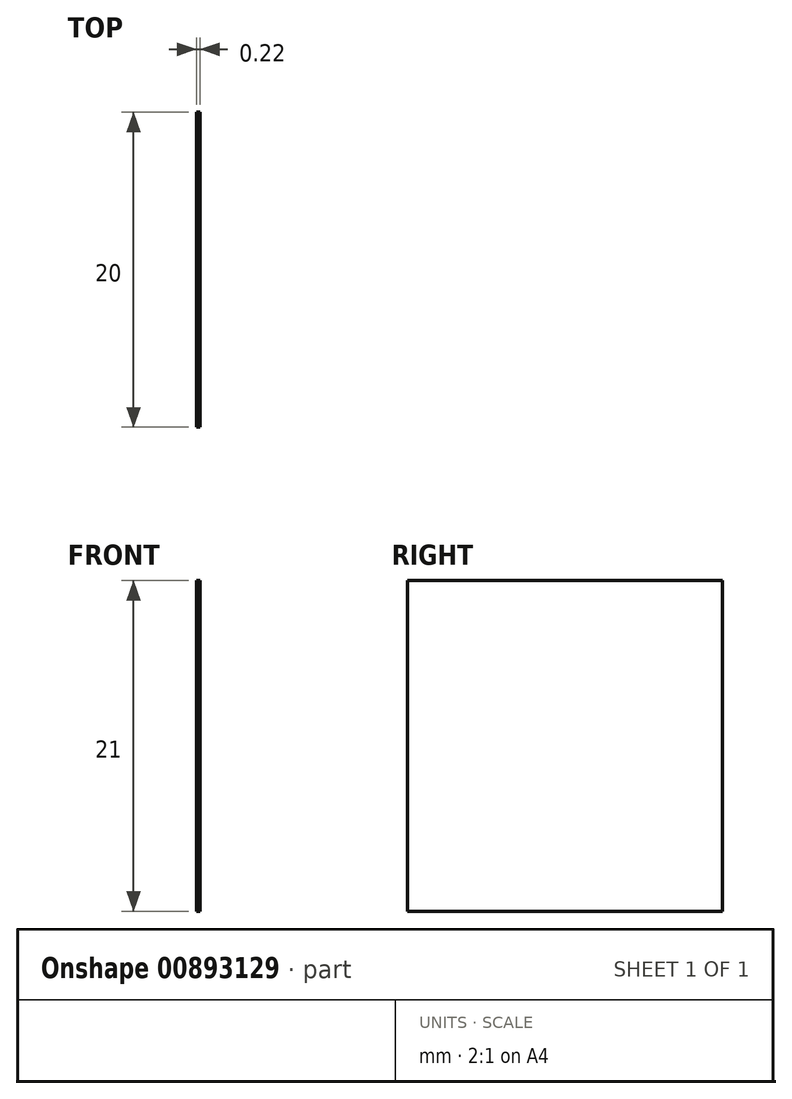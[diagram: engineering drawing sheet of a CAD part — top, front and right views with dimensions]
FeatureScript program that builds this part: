
annotation { "Feature Type Name" : "Feature", "Feature Type Description" : "" }
export const myFeature = defineFeature(function(context is Context, id is Id, definition is map)
    precondition{}
    {
        {
            var Q0;
            Q0=qCreatedBy(makeId("Right.planeOp"),FACE);
            var sketch = newSketch(context, id + "F0", { "sketchPlane" : qUnion([Q0])});
            skLineSegment(sketch, "E0.bottom", {"start": v(0, 0) * mm, "end": v(20, 0) * mm});
            skLineSegment(sketch, "E0.top", {"start": v(0, -21) * mm, "end": v(20, -21) * mm});
            skLineSegment(sketch, "E0.left", {"start": v(0, 0) * mm, "end": v(0, -21) * mm});
            skLineSegment(sketch, "E0.right", {"start": v(20, 0) * mm, "end": v(20, -21) * mm});
            skSolve(sketch);
        }
        {
            var Q0;
            Q0=makeQuery(id+"F0.imprint","IMPRINT",FACE,{"disambiguationData":[TD([[makeQuery(id+"F0.imprint","IMPRINT",EDGE,{"derivedFrom":sQuery(id+"F0.wireOp",EDGE,"E0.bottom")}),-1.0]])]});
            extrude(context, id + "F1", {"entities" : qUnion([Q0]), "depth" : .2220 * mm, "offsetDistance" : 25 * mm});
        }
    });
